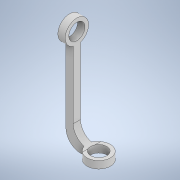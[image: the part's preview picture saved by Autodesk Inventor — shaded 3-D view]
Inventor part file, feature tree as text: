
AUTODESK INVENTOR PART (.ipt)
format: ipt  version: 2022 (Build 260153000, 153)  size: 158,720 bytes
history: native  units: mm
features: extrude x6, sketch x6, other x1, fillet x1
ambient origin geometry x8: Origin, YZ Plane, XZ Plane, XY Plane, X Axis, Y Axis, Z Axis, Center Point
bodies: Body1 (feature_tree)
feature tree (14):
  other  "Bryła1"
  extrude  "Wyciągnięcie proste1"  Depth=22.0mm
  extrude  "Wyciągnięcie proste2"  Depth=5.0mm
  fillet  "Zaokrąglenie1"  Radius=10.0mm
  extrude  "Wyciągnięcie proste3"  Depth=137.0mm
  extrude  "Wyciągnięcie proste4"  Depth=30.0mm
  extrude  "Wyciągnięcie proste5"  Depth=10.0mm
  extrude  "Wyciągnięcie proste6"  Depth=10.0mm
  sketch  "Szkic2"
  sketch  "Szkic4"
  sketch  "Szkic7"
  sketch  "Szkic8"
  sketch  "Szkic9"
  sketch  "Szkic10"
